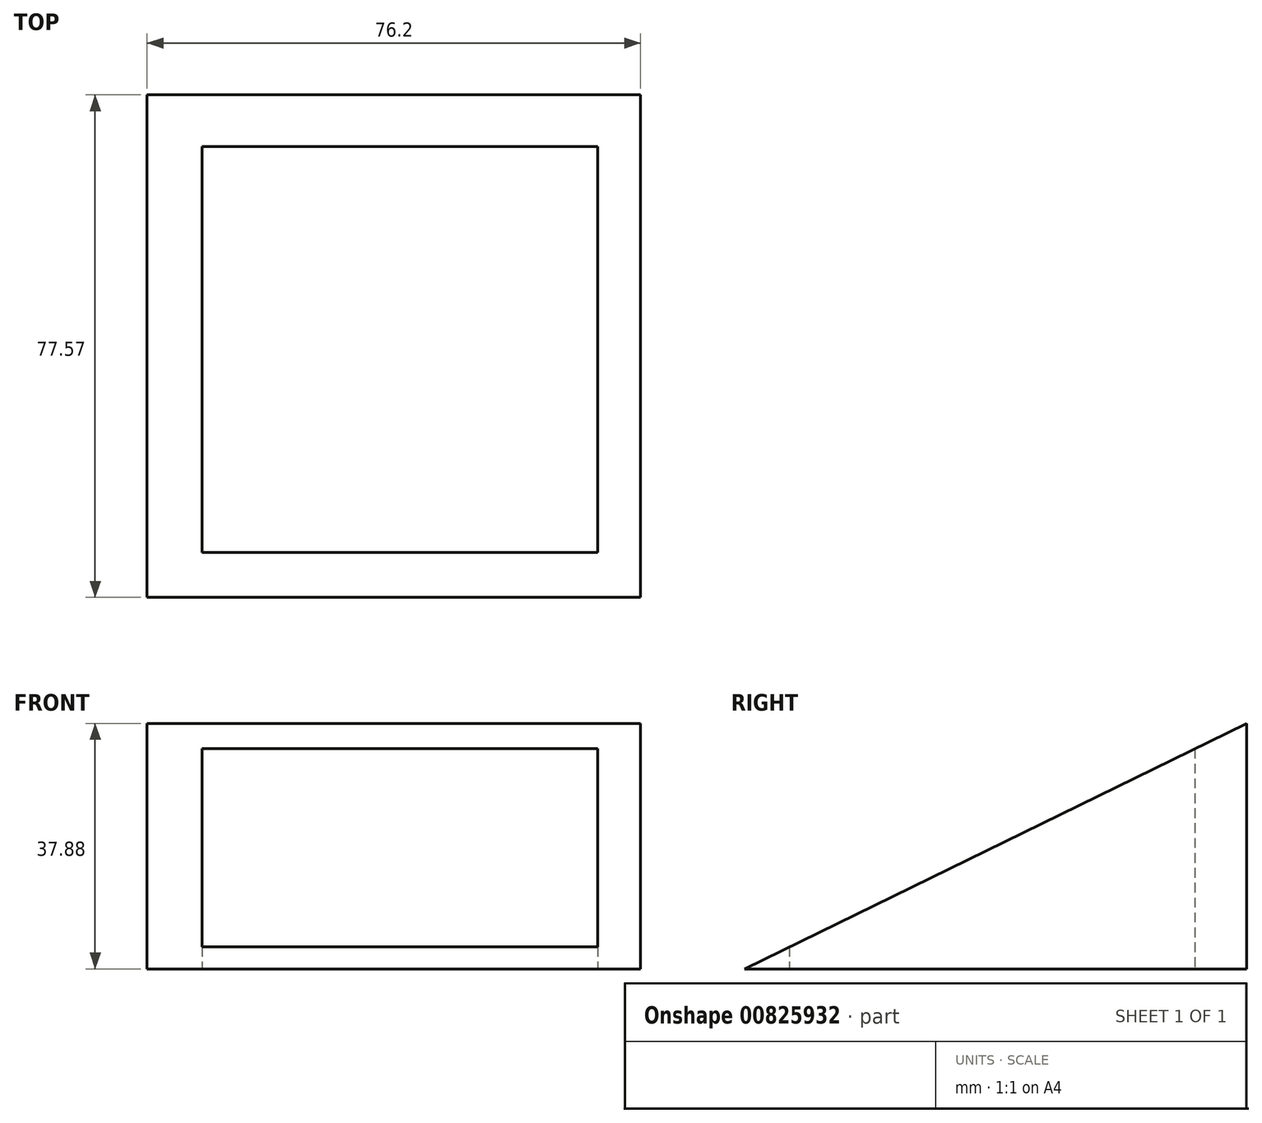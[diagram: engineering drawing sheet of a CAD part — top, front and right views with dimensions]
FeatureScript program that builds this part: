
annotation { "Feature Type Name" : "Feature", "Feature Type Description" : "" }
export const myFeature = defineFeature(function(context is Context, id is Id, definition is map)
    precondition{}
    {
        {
            var Q0;
            Q0=qCreatedBy(makeId("Right.planeOp"),FACE);
            var sketch = newSketch(context, id + "F0", { "sketchPlane" : qUnion([Q0])});
            skLineSegment(sketch, "E0", {"start": v(-40.46, 0) * mm, "end": v(37.11, 0) * mm});
            skLineSegment(sketch, "E1", {"start": v(37.11, 0) * mm, "end": v(37.11, 37.88) * mm});
            skLineSegment(sketch, "E2", {"start": v(37.11, 37.88) * mm, "end": v(-40.46, 0) * mm});
            skSolve(sketch);
        }
        {
            var Q0;
            Q0=makeQuery(id+"F0.imprint","IMPRINT",FACE,{"disambiguationData":[TD([[makeQuery(id+"F0.imprint","IMPRINT",EDGE,{"derivedFrom":sQuery(id+"F0.wireOp",EDGE,"E0")}),1.0]])]});
            extrude(context, id + "F1", {"entities" : qUnion([Q0]), "endBound" : BoundingType.SYMMETRIC, "depth" : 76.2 * mm, "offsetDistance" : 25.4 * mm});
        }
        {
            var Q0;
            Q0=qCreatedBy(makeId("Top.planeOp"),FACE);
            var sketch = newSketch(context, id + "F2", { "sketchPlane" : qUnion([Q0])});
            skLineSegment(sketch, "E3.bottom", {"start": v(-29.65, 29.14) * mm, "end": v(31.45, 29.14) * mm});
            skLineSegment(sketch, "E3.top", {"start": v(-29.65, -33.5) * mm, "end": v(31.45, -33.5) * mm});
            skLineSegment(sketch, "E3.left", {"start": v(-29.65, 29.14) * mm, "end": v(-29.65, -33.5) * mm});
            skLineSegment(sketch, "E3.right", {"start": v(31.45, 29.14) * mm, "end": v(31.45, -33.5) * mm});
            skSolve(sketch);
        }
        {
            var Q0;
            Q0=makeQuery(id+"F2.imprint","IMPRINT",FACE,{"disambiguationData":[TD([[makeQuery(id+"F2.imprint","IMPRINT",EDGE,{"derivedFrom":sQuery(id+"F2.wireOp",EDGE,"E3.bottom")}),-1.0]])]});
            extrude(context, id + "F3", {"entities" : qUnion([Q0]), "operationType" : NewBodyOperationType.REMOVE, "depth" : 76.2 * mm, "offsetDistance" : 25.4 * mm});
        }
    });
